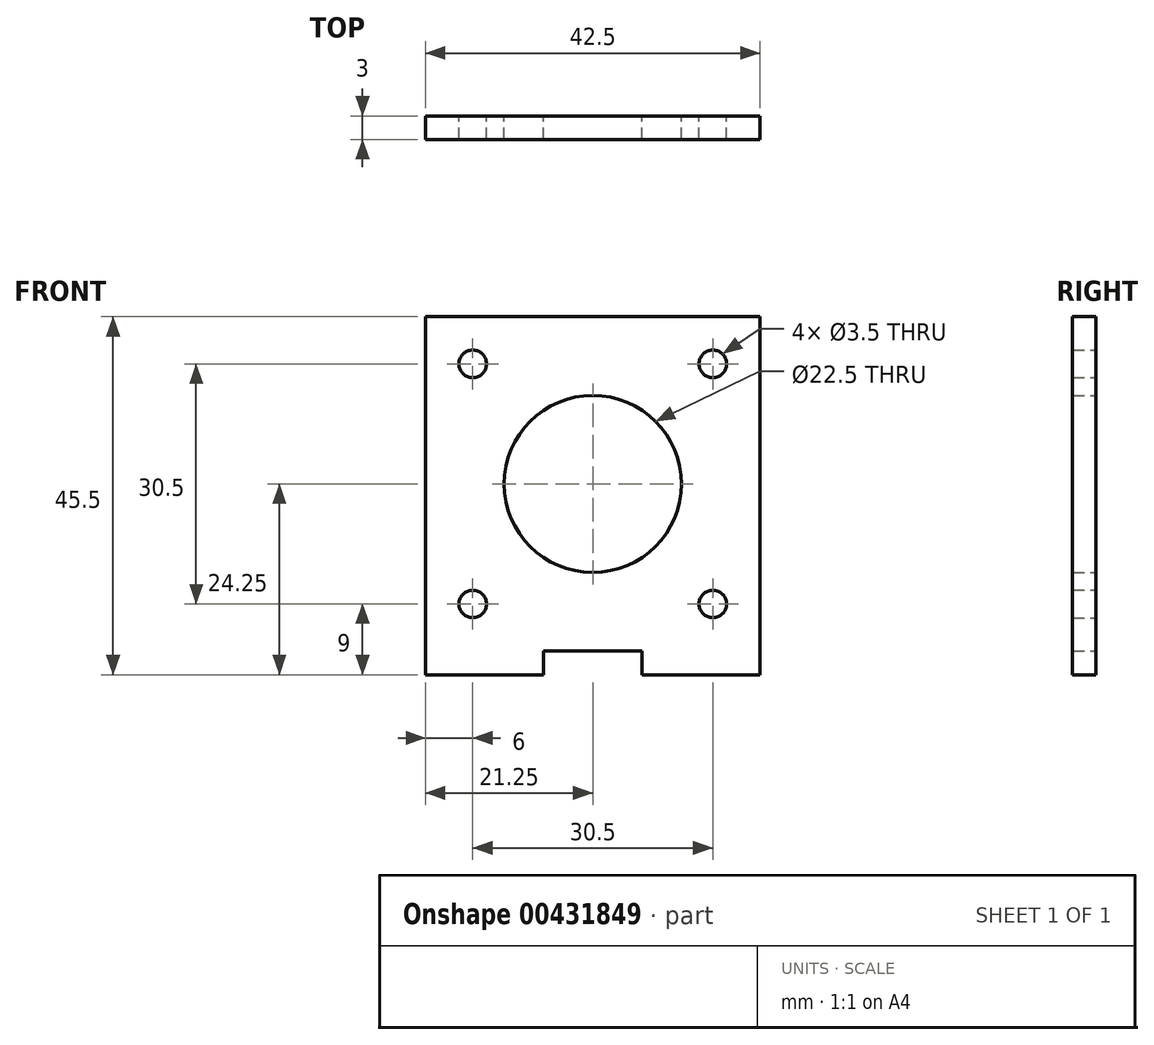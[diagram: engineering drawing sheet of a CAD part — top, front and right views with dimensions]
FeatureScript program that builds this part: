
annotation { "Feature Type Name" : "Feature", "Feature Type Description" : "" }
export const myFeature = defineFeature(function(context is Context, id is Id, definition is map)
    precondition{}
    {
        {
            var Q0;
            Q0=qCreatedBy(makeId("Front.planeOp"),FACE);
            var sketch = newSketch(context, id + "F0", { "sketchPlane" : qUnion([Q0])});
            skLineSegment(sketch, "E0.bottom", {"start": v(15, 0) * mm, "end": v(27.5, 0) * mm});
            skLineSegment(sketch, "E0.top", {"start": v(0, 42.5) * mm, "end": v(42.5, 42.5) * mm});
            skLineSegment(sketch, "E0.left", {"start": v(0, 0) * mm, "end": v(0, 42.5) * mm});
            skLineSegment(sketch, "E0.right", {"start": v(42.5, 0) * mm, "end": v(42.5, 42.5) * mm});
            skCircle(sketch, "E1", {"center": v(21.25, 21.25) * mm, "radius": 11.25 * mm});
            skCircle(sketch, "E2", {"center": v(6, 36.5) * mm, "radius": 1.75 * mm});
            skCircle(sketch, "E3.1.0", {"center": v(-34.6, -13.05) * mm, "radius": 1.75 * mm});
            skCircle(sketch, "E3.2.0", {"center": v(28.6, -23.45) * mm, "radius": 1.75 * mm});
            skPoint(sketch, "E3.center", {"position": v(0, 0) * mm});
            skCircle(sketch, "E4.0.1.0", {"center": v(6, 6) * mm, "radius": 1.75 * mm});
            skCircle(sketch, "E4.1.0.0", {"center": v(36.5, 36.5) * mm, "radius": 1.75 * mm});
            skCircle(sketch, "E4.1.1.0", {"center": v(36.5, 6) * mm, "radius": 1.75 * mm});
            skLineSegment(sketch, "E4.direction1", {"start": v(6, 36.5) * mm, "end": v(36.5, 36.5) * mm, "construction": true});
            skLineSegment(sketch, "E4.direction2", {"start": v(6, 36.5) * mm, "end": v(6, 6) * mm, "construction": true});
            skLineSegment(sketch, "E5.top", {"start": v(0, -3) * mm, "end": v(15, -3) * mm});
            skLineSegment(sketch, "E5.left", {"start": v(0, 0) * mm, "end": v(0, -3) * mm});
            skLineSegment(sketch, "E5.right", {"start": v(15, 0) * mm, "end": v(15, -3) * mm});
            skLineSegment(sketch, "E6.top", {"start": v(42.5, -3) * mm, "end": v(27.5, -3) * mm});
            skLineSegment(sketch, "E6.left", {"start": v(42.5, 0) * mm, "end": v(42.5, -3) * mm});
            skLineSegment(sketch, "E6.right", {"start": v(27.5, 0) * mm, "end": v(27.5, -3) * mm});
            skSolve(sketch);
        }
        {
            var Q0;
            Q0=makeQuery(id+"F0.imprint","IMPRINT",FACE,{"disambiguationData":[TD([[makeQuery(id+"F0.imprint","IMPRINT",EDGE,{"derivedFrom":sQuery(id+"F0.wireOp",EDGE,"E0.bottom")}),1.0]])]});
            extrude(context, id + "F1", {"entities" : qUnion([Q0]), "depth" : 3 * mm});
        }
    });
